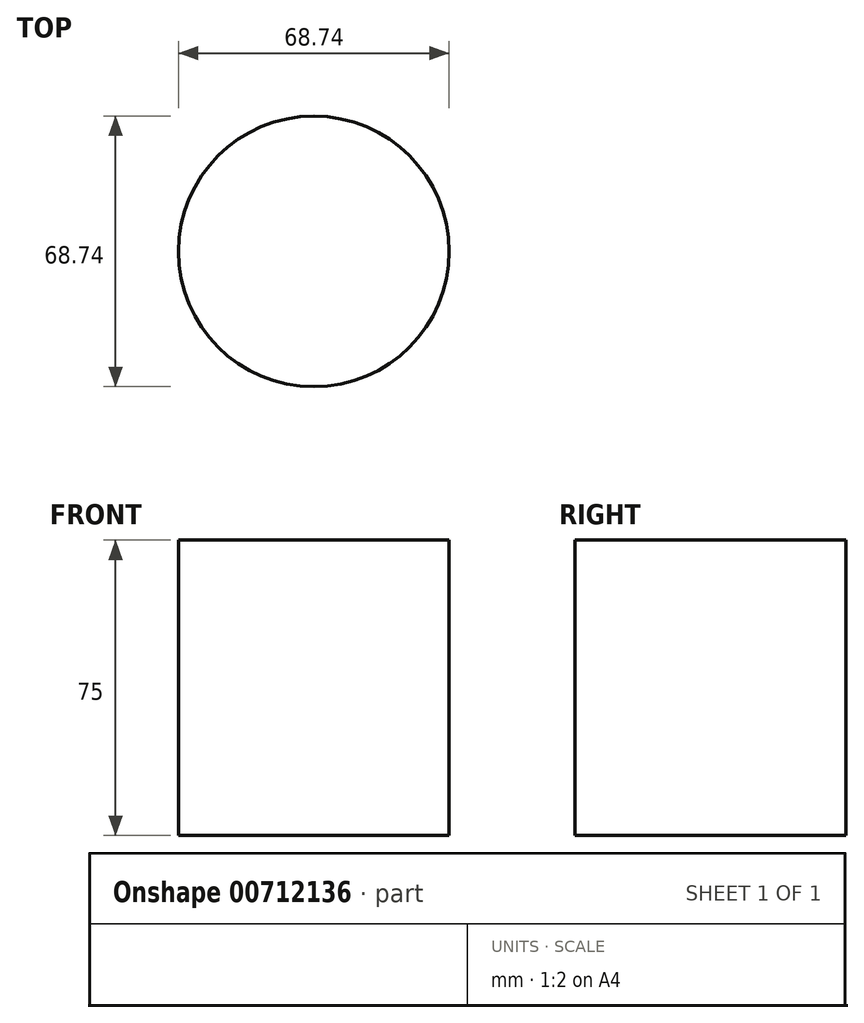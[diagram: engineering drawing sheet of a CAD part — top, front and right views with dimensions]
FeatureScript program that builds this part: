
annotation { "Feature Type Name" : "Feature", "Feature Type Description" : "" }
export const myFeature = defineFeature(function(context is Context, id is Id, definition is map)
    precondition{}
    {
        {
            var Q0;
            Q0=qCreatedBy(makeId("Top.planeOp"),FACE);
            var sketch = newSketch(context, id + "F0", { "sketchPlane" : qUnion([Q0])});
            skCircle(sketch, "E0", {"center": v(0, 0) * mm, "radius": 34.37 * mm});
            skSolve(sketch);
        }
        {
            var Q0;
            Q0 = qSketchRegion(id + "F0", true);
            extrude(context, id + "F1", {"entities" : qUnion([Q0]), "depth" : 75 * mm, "offsetDistance" : 25.4 * mm});
        }
    });
